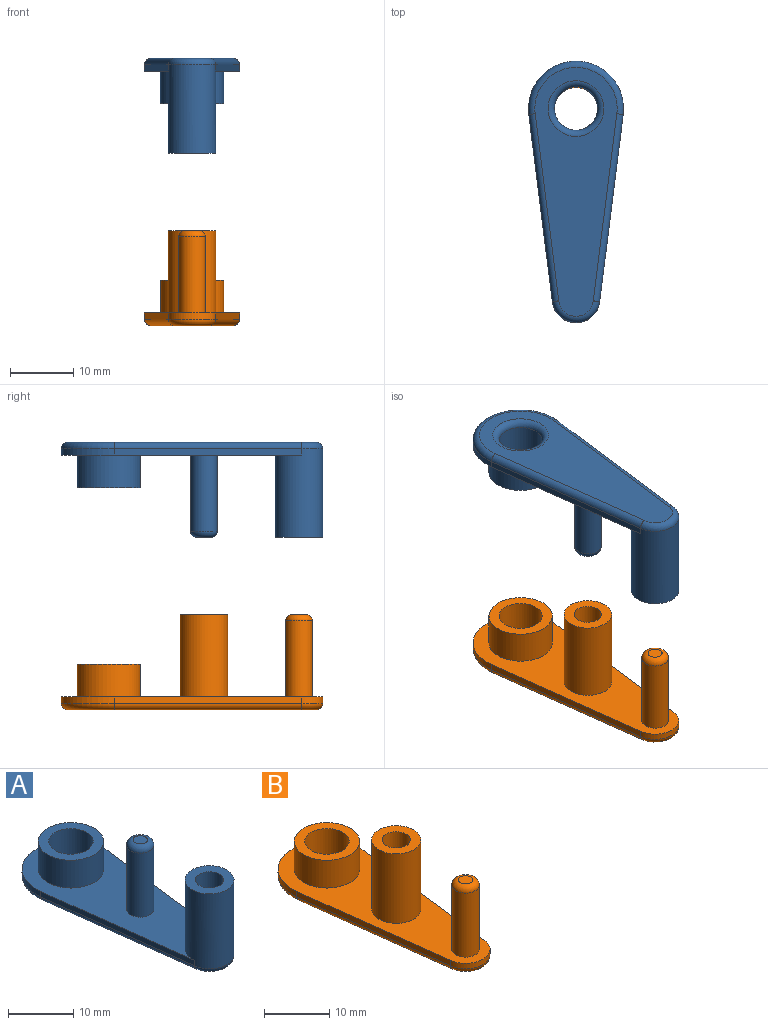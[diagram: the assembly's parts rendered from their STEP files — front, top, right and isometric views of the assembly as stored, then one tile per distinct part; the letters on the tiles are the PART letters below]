
ASSEMBLY  parts=2 mates=1
PART A: 20 faces, bbox 16.2x42.2x15 mm
  f0: plane 37.97x15mm, normal (0,0,1), area 314mm2, adj f1,f2,f3,f4,f7,f12
  f1: cylinder r=3.75mm len=14mm, axis (0,0,1), area 317.1mm2, adj f0,f2,f4,f10,f15
  f2: plane 29.53x3.72mm, normal (0.99,-0.12,0), area 29.8mm2, adj f0,f1,f3,f16
  f3: cylinder r=7.5mm len=15mm, axis (0,0,1), area 25.4mm2, adj f0,f2,f4,f18
  f4: plane 29.53x3.72mm, normal (-0.99,-0.12,0), area 29.8mm2, adj f0,f1,f3,f17
  f5: cylinder r=3.4mm len=6.8mm, axis (0,0,1), area 132.4mm2, adj f8,f19
  f6: plane 39.25x13mm, normal (0,0,-1), area 297.1mm2, adj f15,f16,f17,f18,f19
  f7: cylinder r=5mm len=10mm, axis (0,0,-1), area 163.4mm2, adj f0,f8
  f8: plane 10x10mm, normal (0,0,1), area 42.2mm2, adj f5,f7
  f9: cylinder r=2.15mm len=13mm, axis (0,0,-1), area 175.6mm2, adj f10,f11
  f10: plane 7.5x7.5mm, normal (0,0,1), area 29.7mm2, adj f1,f9
  f11: plane 4.3x4.3mm, normal (0,0,1), area 14.5mm2, adj f9
  f12: cylinder r=2.1mm len=12mm, axis (0,0,-1), area 158.3mm2, adj f0,f14
  f13: plane 2.2x2.2mm, normal (0,0,1), area 3.8mm2, adj f14
  f14: torus R=1.1mm, axis (0,0,1), area 17.1mm2, adj f12,f13
  f15: torus R=2.75mm, axis (0,0,1), area 15.4mm2, adj f1,f6,f16,f17
  f16: cylinder r=1mm len=29.66mm, axis (-0.12,-0.99,0), area 46.8mm2, adj f2,f6,f15,f18
  f17: cylinder r=1mm len=29.66mm, axis (-0.12,0.99,0), area 46.8mm2, adj f4,f6,f15,f18
  f18: torus R=6.5mm, axis (0,0,1), area 38mm2, adj f3,f6,f16,f17
  f19: torus R=4.4mm, axis (0,0,1), area 37.1mm2, adj f5,f6
PART B: 21 faces, bbox 16.2x42.2x15 mm
  f0: cylinder r=3.75mm len=7.44mm, axis (0,0,1), area 10.8mm2, adj f1,f3,f6,f16
  f1: plane 29.53x3.72mm, normal (0.99,-0.12,0), area 29.8mm2, adj f0,f2,f6,f17
  f2: cylinder r=7.5mm len=15mm, axis (0,0,1), area 25.4mm2, adj f1,f3,f6,f19
  f3: plane 29.53x3.72mm, normal (-0.99,-0.12,0), area 29.8mm2, adj f0,f2,f6,f18
  f4: cylinder r=3.4mm len=6.8mm, axis (0,0,1), area 132.4mm2, adj f8,f20
  f5: plane 39.25x13mm, normal (0,0,-1), area 297.1mm2, adj f16,f17,f18,f19,f20
  f6: plane 41.25x15mm, normal (0,0,1), area 314mm2, adj f0,f1,f2,f3,f7,f10,f13
  f7: cylinder r=5mm len=10mm, axis (0,0,-1), area 163.4mm2, adj f6,f8
  f8: plane 10x10mm, normal (0,0,1), area 42.2mm2, adj f4,f7
  f9: cylinder r=2.15mm len=13mm, axis (0,0,-1), area 175.6mm2, adj f11,f12
  f10: cylinder r=3.75mm len=13mm, axis (0,0,-1), area 306.3mm2, adj f6,f11
  f11: plane 7.5x7.5mm, normal (0,0,1), area 29.7mm2, adj f9,f10
  f12: plane 4.3x4.3mm, normal (0,0,1), area 14.5mm2, adj f9
  f13: cylinder r=2.1mm len=12mm, axis (0,0,-1), area 158.3mm2, adj f6,f15
  f14: plane 2.2x2.2mm, normal (0,0,1), area 3.8mm2, adj f15
  f15: torus R=1.1mm, axis (0,0,1), area 17.1mm2, adj f13,f14
  f16: torus R=2.75mm, axis (0,0,1), area 15.4mm2, adj f0,f5,f17,f18
  f17: cylinder r=1mm len=29.66mm, axis (-0.12,-0.99,0), area 46.8mm2, adj f1,f5,f16,f19
  f18: cylinder r=1mm len=29.66mm, axis (-0.12,0.99,0), area 46.8mm2, adj f3,f5,f16,f19
  f19: torus R=6.5mm, axis (0,0,1), area 38mm2, adj f2,f5,f17,f18
  f20: torus R=4.4mm, axis (0,0,1), area 37.1mm2, adj f4,f5
PLACE A rot(axis=(0,1,0),180deg) t=(-0.3,30.03,6.2)mm fixed
PLACE B t=(-0.3,30.03,-31.98)mm
MATE slider A.f12 <-> B.f9  axis (0,0,-1) through (-0.3,15.03,6.2)mm
